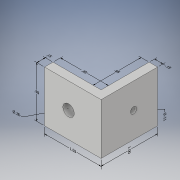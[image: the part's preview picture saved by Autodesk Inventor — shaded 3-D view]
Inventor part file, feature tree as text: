
AUTODESK INVENTOR PART (.ipt)
format: ipt  version: 2018 (Build 220112000, 112)  size: 134,656 bytes
history: native  units: in
note: dims shown in document units (in); Inventor stores cm internally (conversion verified against a paired STEP export)
features: other x10, sketch x3, hole x2, extrude x1
ambient origin geometry x8: Origin, YZ Plane, XZ Plane, XY Plane, X Axis, Y Axis, Z Axis, Center Point
bodies: Solid1 (feature_tree)
feature tree (16):
  other  "Annotations"
  extrude  "Extrusion1"  Depth=0.15in
  hole  "Hole1"  [1 undecoded]
  hole  "Hole2"  [1 undecoded]
  sketch  "Sketch1"  dims[d0=1.0in d1=0.15in]
  sketch  "Sketch2"  dims[d2=0.15in d3=1.0in]
  sketch  "Sketch3"  dims[d4=0.9in d5=0.0in d9=0.425in d10=0.11in d11=0.75in d12=0.375in d13=0.25in d14=0.5635in d15=1.0in d16=0.8108in d17=0.425in d18=0.2in d19=0.75in d20=0.375in d21=0.25in d22=0.5635in d23=1.0in d24=0.8108in d25=0.3469in d26=0.0407in d27=0.15in d28=0.0467in d29=0.0997in d30=0.9in d31=0.3178in d32=0.2872in d33=1.0in d34=0.1415in d35=0.3038in d36=1.0in d37=0.3111in d38=0.1738in d39=0.85in d40=0.1913in d41=0.2198in d42=0.15in d43=0.138in d44=0.0533in d45=0.85in d46=1.4507in d47=0.1934in d48=0.1356in d49=0.2in d50=1.6799in d51=0.294in d52=0.0434in d53=0.11in]
  other  "Linear Dimension 1"
  other  "Linear Dimension 2"
  other  "Linear Dimension 3"
  other  "Linear Dimension 4"
  other  "Linear Dimension 5"
  other  "Linear Dimension 6"
  other  "Linear Dimension 7"
  other  "Diameter Dimension 1"
  other  "Diameter Dimension 2"
note: 2 required parameter values undecoded (feature->parameter linkage not recoverable at this tier; creation-order binding heuristic only, values carry confidence <= 0.55)
